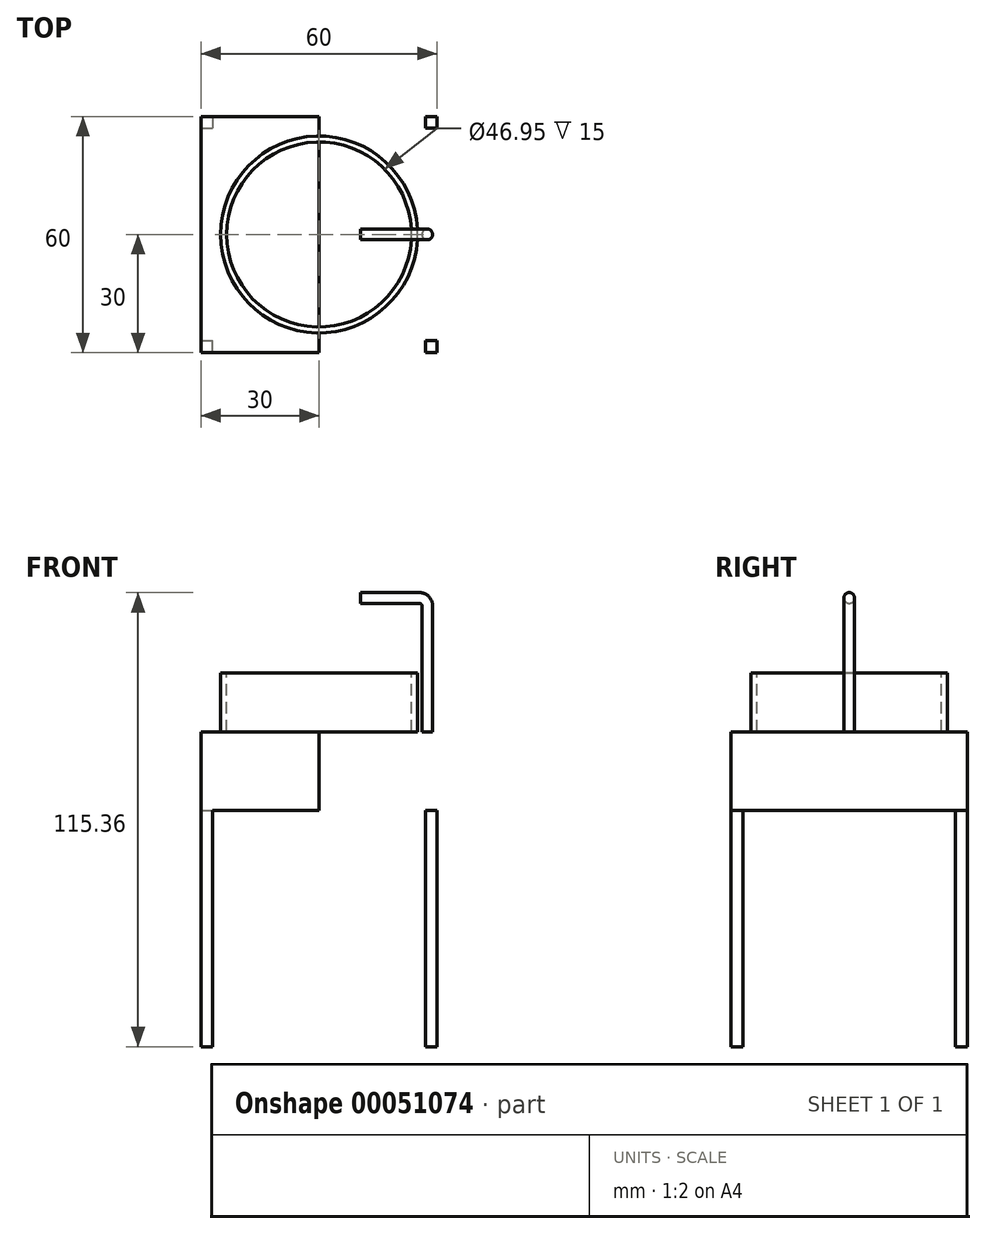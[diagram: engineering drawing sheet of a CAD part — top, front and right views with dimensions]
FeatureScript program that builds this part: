
annotation { "Feature Type Name" : "Feature", "Feature Type Description" : "" }
export const myFeature = defineFeature(function(context is Context, id is Id, definition is map)
    precondition{}
    {
        {
            var Q0;
            Q0=qCreatedBy(makeId("Front.planeOp"),FACE);
            var sketch = newSketch(context, id + "F0", { "sketchPlane" : qUnion([Q0])});
            skLineSegment(sketch, "E0.bottom", {"start": v(0, 0) * mm, "end": v(-25, 0) * mm});
            skLineSegment(sketch, "E0.top", {"start": v(0, 15) * mm, "end": v(-25, 15) * mm});
            skLineSegment(sketch, "E0.left", {"start": v(0, 0) * mm, "end": v(0, 15) * mm});
            skLineSegment(sketch, "E0.right", {"start": v(-25, 0) * mm, "end": v(-25, 15) * mm});
            skSolve(sketch);
        }
        {
            var Q0;
            Q0=makeQuery(id+"F0.imprint","IMPRINT",FACE,{"disambiguationData":[TD([[makeQuery(id+"F0.imprint","IMPRINT",EDGE,{"derivedFrom":sQuery(id+"F0.wireOp",EDGE,"E0.bottom")}),-1.0]])]});
            var Q1;
            Q1=sQuery(id+"F0.wireOp",EDGE,"E0.left");
            revolve(context, id + "F1", {"entities" : qUnion([Q0]), "axis" : qUnion([Q1]), "revolveType" : RevolveType.FULL});
        }
        {
            var Q0;
            Q0=makeQuery(id+"F1.opRevolve","SWEPT_FACE",FACE,{"disambiguationData":[OSD([sQuery(id+"F0.wireOp",EDGE,"E0.top")])]});
            var sketch = newSketch(context, id + "F2", { "sketchPlane" : qUnion([Q0])});
            skCircle(sketch, "E1.0", {"center": v(0, 0) * mm, "radius": 25 * mm});
            skCircle(sketch, "E2.0", {"center": v(0, 0) * mm, "radius": 23.48 * mm});
            skSolve(sketch);
        }
        {
            var Q0;
            Q0=makeQuery(id+"F2.imprint","IMPRINT",FACE,{"disambiguationData":[TD([[makeQuery(id+"F2.imprint","IMPRINT",EDGE,{"derivedFrom":sQuery(id+"F2.wireOp",EDGE,"E2.0")}),1.0]])]});
            extrude(context, id + "F3", {"entities" : qUnion([Q0]), "operationType" : NewBodyOperationType.REMOVE, "oppositeDirection" : true, "depth" : 18.23 * mm});
        }
        {
            var Q0;
            Q0=qCreatedBy(makeId("Front.planeOp"),FACE);
            var sketch = newSketch(context, id + "F4", { "sketchPlane" : qUnion([Q0])});
            skLineSegment(sketch, "E3", {"start": v(0, 0) * mm, "end": v(0, -20) * mm});
            skLineSegment(sketch, "E4", {"start": v(0, 0) * mm, "end": v(30, 0) * mm});
            skLineSegment(sketch, "E5.bottom", {"start": v(30, 0) * mm, "end": v(0, 0) * mm});
            skLineSegment(sketch, "E5.top", {"start": v(30, -20) * mm, "end": v(0, -20) * mm});
            skLineSegment(sketch, "E5.left", {"start": v(30, 0) * mm, "end": v(30, -20) * mm});
            skLineSegment(sketch, "E6.MirrorCS", {"start": v(-30, -20) * mm, "end": v(0, -20) * mm});
            skLineSegment(sketch, "E7.MirrorCS", {"start": v(-30, 0) * mm, "end": v(-30, -20) * mm});
            skLineSegment(sketch, "E8.MirrorCS", {"start": v(-30, 0) * mm, "end": v(0, 0) * mm});
            skSolve(sketch);
        }
        {
            var Q0;
            Q0=makeQuery(id+"F4.imprint","IMPRINT",FACE,{"disambiguationData":[TD([[makeQuery(id+"F4.imprint","IMPRINT",EDGE,{"derivedFrom":sQuery(id+"F4.wireOp",EDGE,"E5.bottom")}),1.0]])]});
            var Q1;
            Q1=makeQuery(id+"F4.imprint","IMPRINT",FACE,{"disambiguationData":[TD([[makeQuery(id+"F4.imprint","IMPRINT",EDGE,{"derivedFrom":sQuery(id+"F4.wireOp",EDGE,"E3")}),-1.0]])]});
            extrude(context, id + "F5", {"entities" : qUnion([Q0, Q1]), "operationType" : NewBodyOperationType.ADD, "depth" : 30 * mm, "hasSecondDirection" : true, "secondDirectionOppositeDirection" : true, "secondDirectionDepth" : 30 * mm});
        }
        {
            var Q0;
            Q0=qCreatedBy(makeId("Front.planeOp"),FACE);
            var sketch = newSketch(context, id + "F6", { "sketchPlane" : qUnion([Q0])});
            skLineSegment(sketch, "E9", {"start": v(27.5, 0) * mm, "end": v(27.5, 32) * mm});
            skLineSegment(sketch, "E10", {"start": v(25.5, 34) * mm, "end": v(10.5, 34) * mm});
            skPoint(sketch, "E11.orphan", {"position": v(24.9, 0) * mm});
            skPoint(sketch, "E12.start.orphan", {"position": v(30.1, 0) * mm});
            skPoint(sketch, "E13.visualSharp", {"position": v(27.5, 34) * mm});
            skArc(sketch, "E13.filletArc", {"start": v(27.5, 32) * mm, "mid": v(26.91, 33.41) * mm, "end": v(25.5, 34) * mm});
            skSolve(sketch);
        }
        {
            var Q0;
            Q0=qCreatedBy(makeId("Top.planeOp"),FACE);
            var sketch = newSketch(context, id + "F7", { "sketchPlane" : qUnion([Q0])});
            skCircle(sketch, "E14", {"center": v(27.5, 0) * mm, "radius": 1.36 * mm});
            skSolve(sketch);
        }
        {
            var Q0;
            Q0=makeQuery(id+"F7.imprint","IMPRINT",FACE,{"disambiguationData":[TD([[makeQuery(id+"F7.imprint","IMPRINT",EDGE,{"derivedFrom":sQuery(id+"F7.wireOp",EDGE,"E14")}),1.0]])]});
            var Q1;
            Q1=sQuery(id+"F6.wireOp",EDGE,"E9");
            var Q2;
            Q2=sQuery(id+"F6.wireOp",EDGE,"E13.filletArc");
            var Q3;
            Q3=sQuery(id+"F6.wireOp",EDGE,"E10");
            sweep(context, id + "F8", {"operationType" : NewBodyOperationType.ADD, "profiles" : qUnion([Q0]), "path" : qUnion([Q1, Q2, Q3])});
        }
        {
            var Q0;
            Q0=makeQuery(id+"F5.opExtrude","SWEPT_FACE",FACE,{"disambiguationData":[OSD([sQuery(id+"F4.wireOp",EDGE,"E5.top"),sQuery(id+"F4.wireOp",EDGE,"E6.MirrorCS")])]});
            var sketch = newSketch(context, id + "F9", { "sketchPlane" : qUnion([Q0])});
            skLineSegment(sketch, "E15.bottom", {"start": v(-30, 30) * mm, "end": v(-27, 30) * mm});
            skLineSegment(sketch, "E15.top", {"start": v(-30, 27) * mm, "end": v(-27, 27) * mm});
            skLineSegment(sketch, "E15.left", {"start": v(-30, 30) * mm, "end": v(-30, 27) * mm});
            skLineSegment(sketch, "E15.right", {"start": v(-27, 30) * mm, "end": v(-27, 27) * mm});
            skLineSegment(sketch, "E16.MirrorCS", {"start": v(30, 27) * mm, "end": v(27, 27) * mm});
            skLineSegment(sketch, "E17.MirrorCS", {"start": v(30, 30) * mm, "end": v(30, 27) * mm});
            skLineSegment(sketch, "E18.MirrorCS", {"start": v(27, 30) * mm, "end": v(27, 27) * mm});
            skLineSegment(sketch, "E19.MirrorCS", {"start": v(30, 30) * mm, "end": v(27, 30) * mm});
            skLineSegment(sketch, "E20.MirrorCS", {"start": v(-30, -27) * mm, "end": v(-27, -27) * mm});
            skLineSegment(sketch, "E21.MirrorCS", {"start": v(-30, -30) * mm, "end": v(-30, -27) * mm});
            skLineSegment(sketch, "E22.MirrorCS", {"start": v(-27, -30) * mm, "end": v(-27, -27) * mm});
            skLineSegment(sketch, "E23.MirrorCS", {"start": v(-30, -30) * mm, "end": v(-27, -30) * mm});
            skLineSegment(sketch, "E24.MirrorCS", {"start": v(30, -27) * mm, "end": v(27, -27) * mm});
            skLineSegment(sketch, "E25.MirrorCS", {"start": v(27, -30) * mm, "end": v(27, -27) * mm});
            skLineSegment(sketch, "E26.MirrorCS", {"start": v(30, -30) * mm, "end": v(27, -30) * mm});
            skLineSegment(sketch, "E27.MirrorCS", {"start": v(30, -30) * mm, "end": v(30, -27) * mm});
            skPoint(sketch, "E28.start.orphan", {"position": v(0, 30) * mm});
            skPoint(sketch, "E29.end.orphan", {"position": v(-30, 0) * mm});
            skSolve(sketch);
        }
        {
            var Q0;
            Q0 = qSketchRegion(id + "F9", true);
            extrude(context, id + "F10", {"entities" : qUnion([Q0]), "operationType" : NewBodyOperationType.ADD, "depth" : 60 * mm});
        }
    });
